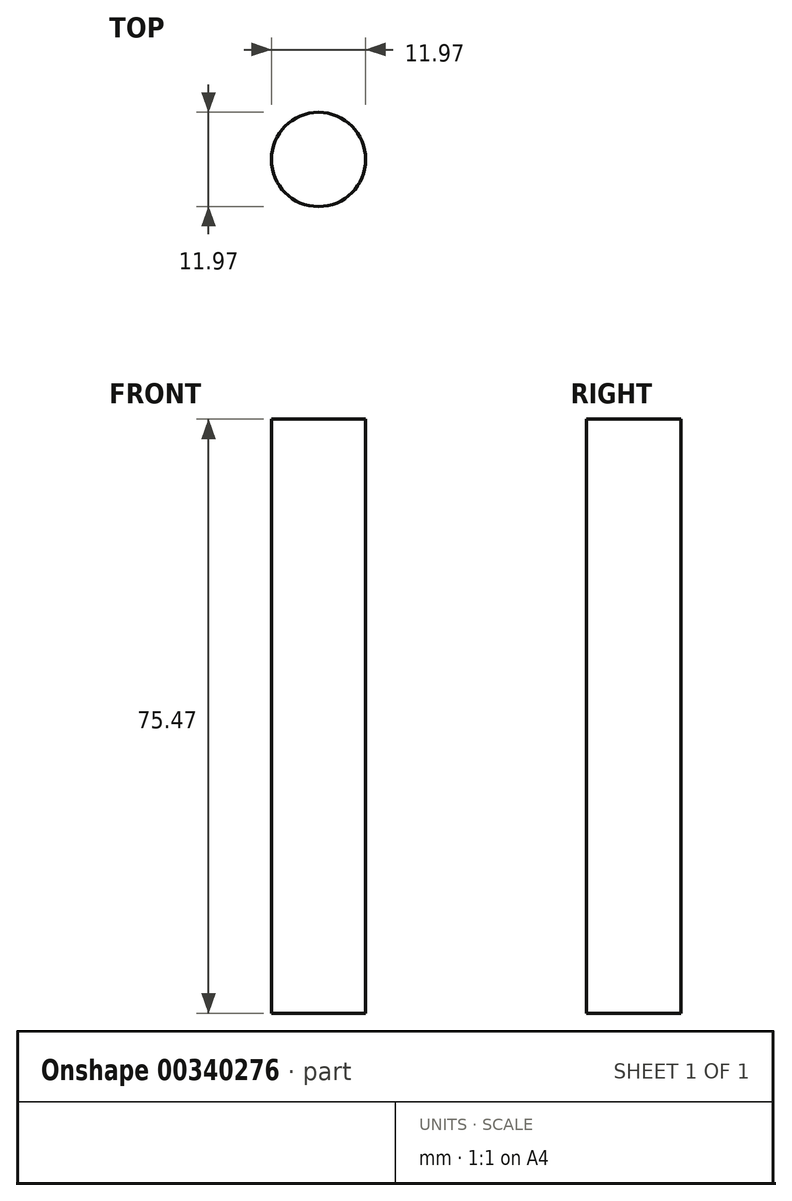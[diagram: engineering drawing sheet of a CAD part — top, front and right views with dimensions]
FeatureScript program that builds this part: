
annotation { "Feature Type Name" : "Feature", "Feature Type Description" : "" }
export const myFeature = defineFeature(function(context is Context, id is Id, definition is map)
    precondition{}
    {
        {
            var Q0;
            Q0=qCreatedBy(makeId("Top.planeOp"),FACE);
            var sketch = newSketch(context, id + "F0", { "sketchPlane" : qUnion([Q0])});
            skCircle(sketch, "E0", {"center": v(29.03, -12.94) * mm, "radius": 5.98 * mm});
            skSolve(sketch);
        }
        {
            var Q0;
            Q0=makeQuery(id+"F0.imprint","IMPRINT",FACE,{"disambiguationData":[TD([[makeQuery(id+"F0.imprint","IMPRINT",EDGE,{"derivedFrom":sQuery(id+"F0.wireOp",EDGE,"E0")}),1.0]])]});
            extrude(context, id + "F1", {"entities" : qUnion([Q0]), "oppositeDirection" : true, "depth" : 75.47 * mm, "hasDraft" : true, "draftAngle" : 0 * degree});
        }
    });
